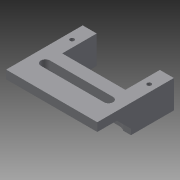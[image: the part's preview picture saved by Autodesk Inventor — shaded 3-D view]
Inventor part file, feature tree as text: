
AUTODESK INVENTOR PART (.ipt)
format: ipt  version: 2015 (Build 190159000, 159)  size: 131,072 bytes
history: native  units: mm
features: extrude x4, sketch x4, hole x2, other x1, chamfer x1
ambient origin geometry x8: Origin, YZ Plane, XZ Plane, XY Plane, X Axis, Y Axis, Z Axis, Center Point
bodies: Body1 (feature_tree)
feature tree (12):
  other  "솔리드1"
  extrude  "돌출1"  Depth=22.5mm
  hole  "구멍1"  [1 undecoded]
  hole  "구멍2"  [1 undecoded]
  extrude  "돌출3"  Depth=10.0mm TaperAngle=0.0deg
  extrude  "돌출4"  Depth=12.0mm TaperAngle=0.0deg
  extrude  "돌출5"  Depth=3.0mm
  chamfer  "모따기1"  Distance=10.0mm
  sketch  "스케치1"
  sketch  "스케치3"
  sketch  "스케치4"
  sketch  "스케치5"
note: 2 required parameter values undecoded (feature->parameter linkage not recoverable at this tier; creation-order binding heuristic only, values carry confidence <= 0.55)
